FCSTD DOCUMENT  (FreeCAD 1.0R39319 (Git))
Label: YR_ASSEMBLED
License: All rights reserved
objects: App::Link×4, App::FeaturePython×4, Assembly::ViewGroup×1, Assembly::JointGroup×1, Assembly::AssemblyObject×1
EXTERNAL_REF file=SSD1322.FCStd obj=ER_OLEDM032_1_new
EXTERNAL_REF file=pin_header_2x08.FCStd obj=Part__Feature
EXTERNAL_REF file=YR1.FCStd obj=Board_ce90
EXTERNAL_REF file=knob.FCStd obj=Body

FEATURE [App::Link] ER_OLEDM032_1_new054  label="ER-OLEDM032-1_new054"
  LinkPlacement = pos=(-1.53778,0.500995,-0.600022) rot=(0,0,0.977807;0rad)
  LinkedObject = -> <external SSD1322.FCStd>#ER_OLEDM032_1_new
  Placement = pos=(-1.53778,0.500995,-0.600022) rot=(0,0,0.977807;0rad)
FEATURE [App::Link] PinHeader_2x08_P254mm_Vertical
  LinkPlacement = pos=(48,12,-1.19209e-07) rot=(0,0,1;0rad)
  LinkedObject = -> <external pin_header_2x08.FCStd>#Part__Feature
  Placement = pos=(48,12,-1.19209e-07) rot=(0,0,1;0rad)
FEATURE [App::Link] YR
  LinkPlacement = pos=(152.25,-62.9999,13) rot=(0,0,1;3.14159rad)
  LinkedObject = -> <external YR1.FCStd>#Board_ce90
  Placement = pos=(152.25,-62.9999,13) rot=(0,0,1;3.14159rad)
FEATURE [App::Link] Body001
  LinkPlacement = pos=(68.75,3.50007,-15) rot=(0,0,1;3.14159rad)
  LinkedObject = -> <external knob.FCStd>#Body
  Placement = pos=(68.75,3.50007,-15) rot=(0,0,1;3.14159rad)
FEATURE [App::FeaturePython] Exploded_View  # WARN: FeaturePython — macro-defined, semantics opaque (R4)
FEATURE [Assembly::ViewGroup] Exploded_Views
  Group = -> [Exploded_View]
FEATURE [App::FeaturePython] Joint  label="Fixed"  # Assembly joint (typed FeaturePython)
  Activated = true
  AngleMax = 0
  AngleMin = 0
  Detach1 = false
  Detach2 = false
  Distance = 0
  Distance2 = 0
  EnableAngleMax = false
  EnableAngleMin = false
  EnableLengthMax = false
  EnableLengthMin = false
  JointType = 0 (Fixed)
  LengthMax = 0
  LengthMin = 0
  Offset2 = pos=(0,0,11) rot=(0,0,1;0rad)
  Placement1 = pos=(83.5,-66.5,0) rot=(0,0,1;0rad)
  Placement2 = pos=(0,0,28) rot=(0,0,1;0rad)
  Reference1 = -> Assembly [YR.Board_Geoms_ce90.Pcb_ce90.Edge287,YR.Board_Geoms_ce90.Pcb_ce90.Edge287]
  Reference2 = -> Assembly [Body001.Edge7,Body001.Edge7]
FEATURE [App::FeaturePython] GroundedJoint001  # Assembly grounded joint (typed FeaturePython)
  ObjectToGround = -> YR
  Placement = pos=(152.25,-62.9999,13) rot=(0,0,1;3.14159rad)
FEATURE [App::FeaturePython] Joint001  label="Fixed001"  # Assembly joint (typed FeaturePython)
  Activated = true
  AngleMax = 0
  AngleMin = 0
  Detach1 = false
  Detach2 = false
  Distance = 0
  Distance2 = 0
  EnableAngleMax = false
  EnableAngleMin = false
  EnableLengthMax = false
  EnableLengthMin = false
  JointType = 0 (Fixed)
  LengthMax = 0
  LengthMin = 0
  Offset2 = pos=(0.125,-0.25,11) rot=(0,0,1;0rad)
  Placement1 = pos=(198.5,-52.5,-1.6) rot=(0,0,1;0rad)
  Placement2 = pos=(-44.7123,-11.0009,12) rot=(0,0,1;3.14159rad)
  Reference1 = -> Assembly [YR.Board_Geoms_ce90.Pcb_ce90.Edge255,YR.Board_Geoms_ce90.Pcb_ce90.Edge255]
  Reference2 = -> Assembly [ER_OLEDM032_1_new054.Part__Feature.Edge249,ER_OLEDM032_1_new054.Part__Feature.Edge249]
FEATURE [Assembly::JointGroup] Joints
  Group = -> [Joint,GroundedJoint001,Joint001]
FEATURE [Assembly::AssemblyObject] Assembly
  Group = -> [Joints,ER_OLEDM032_1_new054,PinHeader_2x08_P254mm_Vertical,YR,Body001,Exploded_Views,Exploded_View,Joint,GroundedJoint001,Joint001]
  Origin = -> Origin001
  Type = Assembly

RESOLVED EXTERNAL PARTS (link-assembly join: the EXTERNAL_REF files above that resolve inside this repo's crawl, each included once):
---- part knob.FCStd = doc fcstd_19e94df1d8a2 ----
FCSTD DOCUMENT  (FreeCAD 1.0R39319 (Git))
Label: knob
License: All rights reserved
LicenseURL: https://en.wikipedia.org/wiki/All_rights_reserved
objects: PartDesign::Chamfer×2, Sketcher::SketchObject×1, PartDesign::Pad×1, PartDesign::Body×1
note: 12 computed .brp shape members not serialized (recipe doc carries the construction recipe); baked Part::Feature solids carry a one-line shape summary decoded from their .brp

FEATURE [Sketcher::SketchObject] Sketch
  ArcFitTolerance = 1e-06
  AttachmentSupport = -> [XY_Plane]
  FullyConstrained = true
  MakeInternals = false
  MapMode = 5
  sketch-geometry (1):
    g0: Circle CenterX=0 CenterY=0 CenterZ=0 NormalX=0 NormalY=0 NormalZ=1 AngleXU=0 Radius=10.5
  constraints (2):
    c: Diameter(g0) = 21
    c: Coincident(g0,g-1)
FEATURE [PartDesign::Pad] Pad
  Direction = (0,0,1)
  Length = 17
  Length2 = 10
  Profile = -> Sketch
  ReferenceAxis = -> Sketch [N_Axis]
  Refine = true
  Suppressed = false
  Type = 0
FEATURE [PartDesign::Chamfer] Chamfer
  Angle = 45
  Base = -> Pad [Edge3]
  BaseFeature = -> Pad
  ChamferType = 0
  FlipDirection = false
  Refine = true
  Size = 1
  Size2 = 1
  SupportTransform = false
  Suppressed = false
  UseAllEdges = false
FEATURE [PartDesign::Chamfer] Chamfer001
  Angle = 45
  Base = -> Chamfer [Edge3]
  BaseFeature = -> Chamfer
  ChamferType = 0
  FlipDirection = false
  Refine = true
  Size = 1
  Size2 = 1
  SupportTransform = false
  Suppressed = false
  UseAllEdges = false
FEATURE [PartDesign::Body] Body
  AllowCompound = false
  Group = -> [Sketch,Pad,Chamfer,Chamfer001]
  Origin = -> Origin
  Tip = -> Chamfer001
